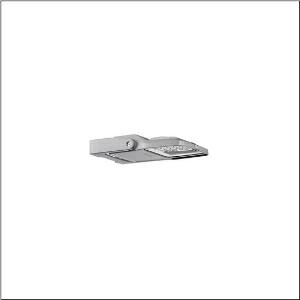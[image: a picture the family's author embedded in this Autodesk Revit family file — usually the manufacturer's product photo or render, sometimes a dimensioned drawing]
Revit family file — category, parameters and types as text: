
# Revit family: floodlight_fl_21_iq_micro___pl61_5xa7761a2c2a_8a4e
name_source: partatom
category: Lighting Fixtures
units: mm (PartAtom-declared; Revit-internal decimal feet)

## family parameters
Cut with Voids When Loaded = No
Host = Face
Light Source = No
Part Type = Normal
Room Calculation Point = No
Round Connector Dimension = Use Diameter
Shared = No

## types (1)
- --- (1 x LED, 2910 lm, 23.1 W, 3000K)
    Apparent Load = 23 VA
    CIE Flux Codes = 33 65 98 100 100
    Color Rendering = 70
    Color Temperature = 3000K
    Default Elevation = 1800 mm
    Description = Floodlight FL 21 iQ micro, floodlight, primary light control with lens, of PMMA, primary optical cover: protective disc, of toughened safety glass, transparent, light distribution: PL61, light emission: direct distribution, installation type: surface-mounted, lamps: LED, High Power LED, rated values: 2.910lm | 23,1W | 126lm/W (begin service life); end service life: 2.910lm | 23,8W; at 50% lumin. flux: 1.455lm | 11W | 132,3lm/W, colour temperature: 3000K, colour rendering: CRI > 70, light colour: 730, light setting 1 begin service life: 100% | 2.910lm | 23,1W | 126lm/W | 3.000K, light setting 1 end service life: 23,8W, further light settings possible, control: optimised constant luminous flux control (CLO 2.0), Desk-Remote (wireless, voltage-free reading and setting of iQ features in the workshop via application-optimized NFC function/RFID function), Light-Fading, Smart-Wire, Night-Set, Lumen-Switch, Temp-Guard, Auto-Match, pre-setting: linear dimming characteristic, with terminal, 6-pole, mains connection: 220..240V, AC, 50/60Hz, luminaire housing, of diecast aluminium, powder-coated, SITECO metallic grey (DB 702S), corrosivity category C5 mid according to DIN EN ISO 12944suitable for swimming poolschlorine-resistant, sealing non-destructively replaceable, design bracket, of diecast aluminium, powder-coated, SITECO metallic grey (DB 702S), protection rating (complete): IP66, insulation class (complete): insulation class II (safety insulation), certification: CE, ENEC, VDE, protection symbol: D, impact resistance: IK07, permissible operating ambient temperature: -40..+40°C, permissible operating ambient temperature for outdoor applications: -40..+50°C, standard: DIN EN 12944, LABS conformity tested according to VDMA 24364:2018-05, packaging unit: 1 piece

Light Distribution: PL61
    Height = 65 mm
    Lamp = 1 x LED
    Lamp Light Flux = 2910 lm
    Lamp Power = 23.1 W
    Lamp count = 1
    Length = 312 mm
    Luminous efficacy = 126 lm/W
    Manufacturer = Siteco
    ModVariant = No
    Model = 5XA7761A2C2A
    Mounting Place = Wall
    Mounting Type = Surface mounted
    Number of Poles = 1
    OnlyDefault = Yes
    Power Factor = 1
    Product Name = Floodlight FL 21 iQ micro | PL61
    Product group = floodlight | wall mounted
    ProductGroupID = 2002
    Protection Class = Protection class II
    Protection Degree = IP 66
    RLX_Detail_Level = 1
    RLX_Emergency_Light_Flux = 0 lm
    RLX_Emergency_Type = 0
    RLX_Emergency_Type_DB = No
    RlxData = <blob elided: 97745 chars, md5=985ad688>
    Socket = socket
    Standby Power = 0 W
    System Light Flux = 2910 lm
    System Power = 23 W
    Type Comments = factory setting: luminous flux: 100 % | dim-lin: 254 | 455 mA
    Type Image = l_1006878.jpg
    URL = http://relux.com
    VarID = @adj_193677
    Voltage = 0 V
    Weight = 0.00 kg
    Width = 230 mm

## geometry (parser evidence)
native form markers: Blend x4, Sweep x13
no freeform markers — native parametric forms only
